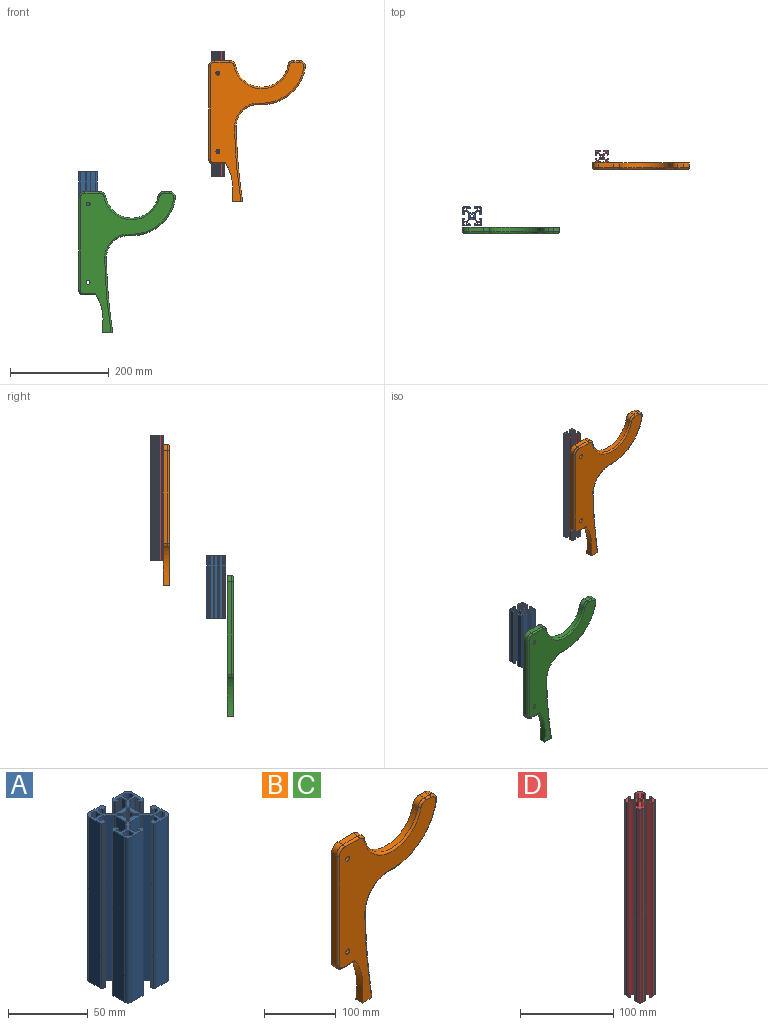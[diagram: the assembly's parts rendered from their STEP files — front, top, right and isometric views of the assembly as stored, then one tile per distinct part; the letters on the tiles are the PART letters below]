
ASSEMBLY  parts=4 mates=2
PART A: 186 faces, bbox 38.1x38.1x127 mm
  f0: plane 127x2.34mm, normal (0,1,0), area 296.8mm2, adj f1,f7,f182,f184
  f1: cylinder r=0.25mm len=127mm, axis (0,0,1), area 50.7mm2, adj f0,f2,f182,f184
  f2: plane 127x4.88mm, normal (1,0,0), area 619.4mm2, adj f1,f3,f182,f184
  f3: cylinder r=0.25mm len=127mm, axis (0,0,1), area 50.7mm2, adj f2,f4,f182,f184
  f4: plane 127x4.88mm, normal (0,-1,0), area 619.4mm2, adj f3,f5,f182,f184
  f5: cylinder r=0.25mm len=127mm, axis (0,0,1), area 50.7mm2, adj f4,f6,f182,f184
  f6: plane 127x2.34mm, normal (-1,0,0), area 296.8mm2, adj f5,f7,f182,f184
  f7: cylinder r=2.79mm len=127mm, axis (0,0,1), area 557.4mm2, adj f0,f6,f182,f184
  f8: plane 127x3.56mm, normal (0,1,0), area 452.4mm2, adj f9,f127,f182,f184
  f9: cylinder r=0.89mm len=127mm, axis (0,0,1), area 177.3mm2, adj f8,f10,f182,f184
  f10: plane 127x2.29mm, normal (1,0,0), area 290.3mm2, adj f9,f11,f182,f184
  f11: cylinder r=0.25mm len=127mm, axis (0,0,1), area 50.7mm2, adj f10,f12,f182,f184
  f12: plane 127x1.35mm, normal (0,-1,0), area 171mm2, adj f11,f13,f182,f184
  f13: cylinder r=0.25mm len=127mm, axis (0,0,1), area 50.7mm2, adj f12,f14,f182,f184
  f14: plane 127x0.98mm, normal (1,0,0), area 124.3mm2, adj f13,f15,f182,f184
  f15: cylinder r=1.57mm len=127mm, axis (0,0,1), area 314.2mm2, adj f14,f16,f182,f184
  f16: plane 127x0.91mm, normal (0,1,0), area 116.1mm2, adj f15,f17,f182,f184
  f17: cylinder r=1.57mm len=127mm, axis (0,0,1), area 314.2mm2, adj f16,f18,f182,f184
  f18: plane 127x10.24mm, normal (-1,0,0), area 1300mm2, adj f17,f19,f182,f184
  f19: cylinder r=3.17mm len=127mm, axis (0,0,1), area 633.4mm2, adj f18,f20,f182,f184
  f20: plane 127x10.24mm, normal (0,-1,0), area 1300mm2, adj f19,f21,f182,f184
  f21: cylinder r=1.57mm len=127mm, axis (0,0,1), area 314.2mm2, adj f20,f22,f182,f184
  f22: plane 127x0.91mm, normal (1,0,0), area 116.1mm2, adj f21,f23,f182,f184
  f23: cylinder r=1.57mm len=127mm, axis (0,0,1), area 314.2mm2, adj f22,f24,f182,f184
  f24: plane 127x0.98mm, normal (0,1,0), area 124.3mm2, adj f23,f25,f182,f184
  f25: cylinder r=0.25mm len=127mm, axis (0,0,1), area 50.7mm2, adj f24,f26,f182,f184
  f26: plane 127x1.35mm, normal (-1,0,0), area 171mm2, adj f25,f27,f182,f184
  f27: cylinder r=0.25mm len=127mm, axis (0,0,1), area 50.7mm2, adj f26,f28,f182,f184
  f28: plane 127x2.29mm, normal (0,1,0), area 290.3mm2, adj f27,f29,f182,f184
  f29: cylinder r=0.89mm len=127mm, axis (0,0,1), area 177.3mm2, adj f28,f30,f182,f184
  f30: plane 127x3.56mm, normal (1,0,0), area 452.4mm2, adj f29,f31,f182,f184
  f31: cylinder r=1.27mm len=127mm, axis (0,0,1), area 126.7mm2, adj f30,f32,f182,f184
  f32: plane 127x4.38mm, normal (0.71,-0.71,0), area 785.9mm2, adj f31,f33,f182,f184
  f33: cylinder r=1.27mm len=127mm, axis (0,0,1), area 126.7mm2, adj f32,f34,f182,f184
  f34: plane 127x9.31mm, normal (0,-1,0), area 1182.4mm2, adj f33,f35,f182,f184
  f35: cylinder r=1.27mm len=127mm, axis (0,0,1), area 126.7mm2, adj f34,f36,f182,f184
  f36: plane 127x4.38mm, normal (-0.71,-0.71,0), area 785.9mm2, adj f35,f37,f182,f184
  f37: cylinder r=1.27mm len=127mm, axis (0,0,1), area 126.7mm2, adj f36,f38,f182,f184
  f38: plane 127x3.56mm, normal (-1,0,0), area 452.4mm2, adj f37,f39,f182,f184
  f39: cylinder r=0.89mm len=127mm, axis (0,0,1), area 177.3mm2, adj f38,f40,f182,f184
  f40: plane 127x2.29mm, normal (0,1,0), area 290.3mm2, adj f39,f41,f182,f184
  f41: cylinder r=0.25mm len=127mm, axis (0,0,1), area 50.7mm2, adj f40,f42,f182,f184
  f42: plane 127x1.35mm, normal (1,0,0), area 171mm2, adj f41,f43,f182,f184
  f43: cylinder r=0.25mm len=127mm, axis (0,0,1), area 50.7mm2, adj f42,f44,f182,f184
  f44: plane 127x0.98mm, normal (0,1,0), area 124.3mm2, adj f43,f45,f182,f184
  f45: cylinder r=1.57mm len=127mm, axis (0,0,1), area 314.2mm2, adj f44,f46,f182,f184
  f46: plane 127x0.91mm, normal (-1,0,0), area 116.1mm2, adj f45,f47,f182,f184
  f47: cylinder r=1.57mm len=127mm, axis (0,0,1), area 314.2mm2, adj f46,f48,f182,f184
  f48: plane 127x10.24mm, normal (0,-1,0), area 1300mm2, adj f47,f49,f182,f184
  f49: cylinder r=3.17mm len=127mm, axis (0,0,1), area 633.4mm2, adj f48,f50,f182,f184
  f50: plane 127x10.24mm, normal (1,0,0), area 1300mm2, adj f49,f51,f182,f184
  f51: cylinder r=1.57mm len=127mm, axis (0,0,1), area 314.2mm2, adj f50,f52,f182,f184
  f52: plane 127x0.91mm, normal (0,1,0), area 116.1mm2, adj f51,f53,f182,f184
  f53: cylinder r=1.57mm len=127mm, axis (0,0,1), area 314.2mm2, adj f52,f54,f182,f184
  f54: plane 127x0.98mm, normal (-1,0,0), area 124.3mm2, adj f53,f55,f182,f184
  f55: cylinder r=0.25mm len=127mm, axis (0,0,1), area 50.7mm2, adj f54,f56,f182,f184
  f56: plane 127x1.35mm, normal (0,-1,0), area 171mm2, adj f55,f57,f182,f184
  f57: cylinder r=0.25mm len=127mm, axis (0,0,1), area 50.7mm2, adj f56,f58,f182,f184
  f58: plane 127x2.29mm, normal (-1,0,0), area 290.3mm2, adj f57,f59,f182,f184
  f59: cylinder r=0.89mm len=127mm, axis (0,0,1), area 177.3mm2, adj f58,f60,f182,f184
  f60: plane 127x3.56mm, normal (0,1,0), area 452.4mm2, adj f59,f61,f182,f184
  f61: cylinder r=1.27mm len=127mm, axis (0,0,1), area 126.7mm2, adj f60,f62,f182,f184
  f62: plane 127x4.38mm, normal (0.71,0.71,0), area 785.9mm2, adj f61,f63,f182,f184
  f63: cylinder r=1.27mm len=127mm, axis (0,0,1), area 126.7mm2, adj f62,f64,f182,f184
  f64: plane 127x9.31mm, normal (1,0,0), area 1182.4mm2, adj f63,f65,f182,f184
  f65: cylinder r=1.27mm len=127mm, axis (0,0,1), area 126.7mm2, adj f64,f66,f182,f184
  f66: plane 127x4.38mm, normal (0.71,-0.71,0), area 785.9mm2, adj f65,f67,f182,f184
  f67: cylinder r=1.27mm len=127mm, axis (0,0,1), area 126.7mm2, adj f66,f68,f182,f184
  f68: plane 127x3.56mm, normal (0,-1,0), area 452.4mm2, adj f67,f69,f182,f184
  f69: cylinder r=0.89mm len=127mm, axis (0,0,1), area 177.3mm2, adj f68,f70,f182,f184
  f70: plane 127x2.29mm, normal (-1,0,0), area 290.3mm2, adj f69,f71,f182,f184
  f71: cylinder r=0.25mm len=127mm, axis (0,0,1), area 50.7mm2, adj f70,f72,f182,f184
  f72: plane 127x1.35mm, normal (0,1,0), area 171mm2, adj f71,f73,f182,f184
  f73: cylinder r=0.25mm len=127mm, axis (0,0,1), area 50.7mm2, adj f72,f74,f182,f184
  f74: plane 127x0.98mm, normal (-1,0,0), area 124.3mm2, adj f73,f75,f182,f184
  f75: cylinder r=1.57mm len=127mm, axis (0,0,1), area 314.2mm2, adj f74,f76,f182,f184
  f76: plane 127x0.91mm, normal (0,-1,0), area 116.1mm2, adj f75,f77,f182,f184
  f77: cylinder r=1.57mm len=127mm, axis (0,0,1), area 314.2mm2, adj f76,f78,f182,f184
  f78: plane 127x10.24mm, normal (1,0,0), area 1300mm2, adj f77,f79,f182,f184
  f79: cylinder r=3.17mm len=127mm, axis (0,0,1), area 633.4mm2, adj f78,f80,f182,f184
  f80: plane 127x10.24mm, normal (0,1,0), area 1300mm2, adj f79,f81,f182,f184
  f81: cylinder r=1.57mm len=127mm, axis (0,0,1), area 314.2mm2, adj f80,f82,f182,f184
  f82: plane 127x0.91mm, normal (-1,0,0), area 116.1mm2, adj f81,f83,f182,f184
  f83: cylinder r=1.57mm len=127mm, axis (0,0,1), area 314.2mm2, adj f82,f84,f182,f184
  f84: plane 127x0.98mm, normal (0,-1,0), area 124.3mm2, adj f83,f85,f182,f184
  f85: cylinder r=0.25mm len=127mm, axis (0,0,1), area 50.7mm2, adj f84,f86,f182,f184
  f86: plane 127x1.35mm, normal (1,0,0), area 171mm2, adj f85,f87,f182,f184
  f87: cylinder r=0.25mm len=127mm, axis (0,0,1), area 50.7mm2, adj f86,f88,f182,f184
  f88: plane 127x2.29mm, normal (0,-1,0), area 290.3mm2, adj f87,f89,f182,f184
  f89: cylinder r=0.89mm len=127mm, axis (0,0,1), area 177.3mm2, adj f88,f90,f182,f184
  f90: plane 127x3.56mm, normal (-1,0,0), area 452.4mm2, adj f89,f91,f182,f184
  f91: cylinder r=1.27mm len=127mm, axis (0,0,1), area 126.7mm2, adj f90,f92,f182,f184
  f92: plane 127x4.38mm, normal (-0.71,0.71,0), area 785.9mm2, adj f91,f93,f182,f184
  f93: cylinder r=1.27mm len=127mm, axis (0,0,1), area 126.7mm2, adj f92,f94,f182,f184
  f94: plane 127x9.31mm, normal (0,1,0), area 1182.4mm2, adj f93,f95,f182,f184
  f95: cylinder r=1.27mm len=127mm, axis (0,0,1), area 126.7mm2, adj f94,f96,f182,f184
  f96: plane 127x4.38mm, normal (0.71,0.71,0), area 785.9mm2, adj f95,f97,f182,f184
  f97: cylinder r=1.27mm len=127mm, axis (0,0,1), area 126.7mm2, adj f96,f98,f182,f184
  f98: plane 127x3.56mm, normal (1,0,0), area 452.4mm2, adj f97,f99,f182,f184
  f99: cylinder r=0.89mm len=127mm, axis (0,0,1), area 177.3mm2, adj f98,f100,f182,f184
  f100: plane 127x2.29mm, normal (0,-1,0), area 290.3mm2, adj f99,f101,f182,f184
  f101: cylinder r=0.25mm len=127mm, axis (0,0,1), area 50.7mm2, adj f100,f102,f182,f184
  f102: plane 127x1.35mm, normal (-1,0,0), area 171mm2, adj f101,f103,f182,f184
  f103: cylinder r=0.25mm len=127mm, axis (0,0,1), area 50.7mm2, adj f102,f104,f182,f184
  f104: plane 127x0.98mm, normal (0,-1,0), area 124.3mm2, adj f103,f105,f182,f184
  f105: cylinder r=1.57mm len=127mm, axis (0,0,1), area 314.2mm2, adj f104,f106,f182,f184
  f106: plane 127x0.91mm, normal (1,0,0), area 116.1mm2, adj f105,f107,f182,f184
  f107: cylinder r=1.57mm len=127mm, axis (0,0,1), area 314.2mm2, adj f106,f108,f182,f184
  f108: plane 127x10.24mm, normal (0,1,0), area 1300mm2, adj f107,f109,f182,f184
  f109: cylinder r=3.17mm len=127mm, axis (0,0,1), area 633.4mm2, adj f108,f110,f182,f184
  f110: plane 127x10.24mm, normal (-1,0,0), area 1300mm2, adj f109,f111,f182,f184
  f111: cylinder r=1.57mm len=127mm, axis (0,0,1), area 314.2mm2, adj f110,f112,f182,f184
  f112: plane 127x0.91mm, normal (0,-1,0), area 116.1mm2, adj f111,f113,f182,f184
  f113: cylinder r=1.57mm len=127mm, axis (0,0,1), area 314.2mm2, adj f112,f114,f182,f184
  f114: plane 127x0.98mm, normal (1,0,0), area 124.3mm2, adj f113,f115,f182,f184
  f115: cylinder r=0.25mm len=127mm, axis (0,0,1), area 50.7mm2, adj f114,f116,f182,f184
  f116: plane 127x1.35mm, normal (0,1,0), area 171mm2, adj f115,f117,f182,f184
  f117: cylinder r=0.25mm len=127mm, axis (0,0,1), area 50.7mm2, adj f116,f118,f182,f184
  f118: plane 127x2.29mm, normal (1,0,0), area 290.3mm2, adj f117,f119,f182,f184
  f119: cylinder r=0.89mm len=127mm, axis (0,0,1), area 177.3mm2, adj f118,f120,f182,f184
  f120: plane 127x3.56mm, normal (0,-1,0), area 452.4mm2, adj f119,f121,f182,f184
  f121: cylinder r=1.27mm len=127mm, axis (0,0,1), area 126.7mm2, adj f120,f122,f182,f184
  f122: plane 127x4.38mm, normal (-0.71,-0.71,0), area 785.9mm2, adj f121,f123,f182,f184
  f123: cylinder r=1.27mm len=127mm, axis (0,0,1), area 126.7mm2, adj f122,f124,f182,f184
  f124: plane 127x9.31mm, normal (-1,0,0), area 1182.4mm2, adj f123,f125,f182,f184
  f125: cylinder r=1.27mm len=127mm, axis (0,0,1), area 126.7mm2, adj f124,f126,f182,f184
  f126: plane 127x4.38mm, normal (-0.71,0.71,0), area 785.9mm2, adj f125,f127,f182,f184
  f127: cylinder r=1.27mm len=127mm, axis (0,0,1), area 126.7mm2, adj f8,f126,f182,f184
  f128: plane 127x4.88mm, normal (0,1,0), area 619.4mm2, adj f129,f135,f182,f184
  f129: cylinder r=0.25mm len=127mm, axis (0,0,1), area 50.7mm2, adj f128,f130,f182,f184
  f130: plane 127x2.34mm, normal (1,0,0), area 296.8mm2, adj f129,f131,f182,f184
  f131: cylinder r=2.79mm len=127mm, axis (0,0,1), area 557.4mm2, adj f130,f132,f182,f184
  f132: plane 127x2.34mm, normal (0,-1,0), area 296.8mm2, adj f131,f133,f182,f184
  f133: cylinder r=0.25mm len=127mm, axis (0,0,1), area 50.7mm2, adj f132,f134,f182,f184
  f134: plane 127x4.88mm, normal (-1,0,0), area 619.4mm2, adj f133,f135,f182,f184
  f135: cylinder r=0.25mm len=127mm, axis (0,0,1), area 50.7mm2, adj f128,f134,f182,f184
  f136: plane 127x4.88mm, normal (-1,0,0), area 619.4mm2, adj f137,f143,f182,f184
  f137: cylinder r=0.25mm len=127mm, axis (0,0,1), area 50.7mm2, adj f136,f138,f182,f184
  f138: plane 127x2.34mm, normal (0,1,0), area 296.8mm2, adj f137,f139,f182,f184
  f139: cylinder r=2.79mm len=127mm, axis (0,0,1), area 557.4mm2, adj f138,f140,f182,f184
  f140: plane 127x2.34mm, normal (1,0,0), area 296.8mm2, adj f139,f141,f182,f184
  f141: cylinder r=0.25mm len=127mm, axis (0,0,1), area 50.7mm2, adj f140,f142,f182,f184
  f142: plane 127x4.88mm, normal (0,-1,0), area 619.4mm2, adj f141,f143,f182,f184
  f143: cylinder r=0.25mm len=127mm, axis (0,0,1), area 50.7mm2, adj f136,f142,f182,f184
  f144: plane 127x1.89mm, normal (0.71,-0.71,0), area 339.6mm2, adj f145,f175,f182,f184
  f145: cylinder r=3.33mm len=127mm, axis (0,0,1), area 367.4mm2, adj f144,f146,f182,f184
  f146: plane 127x1.89mm, normal (0.71,0.71,0), area 339.6mm2, adj f145,f147,f182,f184
  f147: cylinder r=0.89mm len=127mm, axis (0,0,1), area 88.7mm2, adj f146,f148,f182,f184
  f148: plane 127x0.99mm, normal (1,0,0), area 126.3mm2, adj f147,f149,f182,f184
  f149: cylinder r=0.25mm len=127mm, axis (0,0,1), area 50.7mm2, adj f148,f150,f182,f184
  f150: plane 127x0.99mm, normal (0,-1,0), area 126.3mm2, adj f149,f151,f182,f184
  f151: cylinder r=0.89mm len=127mm, axis (0,0,1), area 88.7mm2, adj f150,f152,f182,f184
  f152: plane 127x1.89mm, normal (-0.71,-0.71,0), area 339.6mm2, adj f151,f153,f182,f184
  f153: cylinder r=3.33mm len=127mm, axis (0,0,1), area 367.4mm2, adj f152,f154,f182,f184
  f154: plane 127x1.89mm, normal (0.71,-0.71,0), area 339.6mm2, adj f153,f155,f182,f184
  f155: cylinder r=0.89mm len=127mm, axis (0,0,1), area 88.7mm2, adj f154,f156,f182,f184
  f156: plane 127x0.99mm, normal (0,-1,0), area 126.3mm2, adj f155,f157,f182,f184
  f157: cylinder r=0.25mm len=127mm, axis (0,0,1), area 50.7mm2, adj f156,f158,f182,f184
  f158: plane 127x0.99mm, normal (-1,0,0), area 126.3mm2, adj f157,f159,f182,f184
  f159: cylinder r=0.89mm len=127mm, axis (0,0,1), area 88.7mm2, adj f158,f160,f182,f184
  f160: plane 127x1.89mm, normal (-0.71,0.71,0), area 339.6mm2, adj f159,f161,f182,f184
  f161: cylinder r=3.33mm len=127mm, axis (0,0,1), area 367.4mm2, adj f160,f162,f182,f184
  f162: plane 127x1.89mm, normal (-0.71,-0.71,0), area 339.6mm2, adj f161,f163,f182,f184
  f163: cylinder r=0.89mm len=127mm, axis (0,0,1), area 88.7mm2, adj f162,f164,f182,f184
  f164: plane 127x0.99mm, normal (-1,0,0), area 126.3mm2, adj f163,f165,f182,f184
  f165: cylinder r=0.25mm len=127mm, axis (0,0,1), area 50.7mm2, adj f164,f166,f182,f184
  f166: plane 127x0.99mm, normal (0,1,0), area 126.3mm2, adj f165,f167,f182,f184
  f167: cylinder r=0.89mm len=127mm, axis (0,0,1), area 88.7mm2, adj f166,f168,f182,f184
  f168: plane 127x1.89mm, normal (0.71,0.71,0), area 339.6mm2, adj f167,f169,f182,f184
  f169: cylinder r=3.33mm len=127mm, axis (0,0,1), area 367.4mm2, adj f168,f170,f182,f184
  f170: plane 127x1.89mm, normal (-0.71,0.71,0), area 339.6mm2, adj f169,f171,f182,f184
  f171: cylinder r=0.89mm len=127mm, axis (0,0,1), area 88.7mm2, adj f170,f172,f182,f184
  f172: plane 127x0.99mm, normal (0,1,0), area 126.3mm2, adj f171,f173,f182,f184
  f173: cylinder r=0.25mm len=127mm, axis (0,0,1), area 50.7mm2, adj f172,f174,f182,f184
  f174: plane 127x0.99mm, normal (1,0,0), area 126.3mm2, adj f173,f175,f182,f184
  f175: cylinder r=0.89mm len=127mm, axis (0,0,1), area 88.7mm2, adj f144,f174,f182,f184
  f176: plane 127x4.88mm, normal (0,1,0), area 619.4mm2, adj f177,f181,f182,f184
  f177: cylinder r=0.25mm len=127mm, axis (0,0,1), area 50.7mm2, adj f176,f178,f182,f184
  f178: plane 127x4.88mm, normal (1,0,0), area 619.4mm2, adj f177,f179,f182,f184
  f179: cylinder r=0.25mm len=127mm, axis (0,0,1), area 50.7mm2, adj f178,f180,f182,f184
  f180: plane 127x2.34mm, normal (0,-1,0), area 296.8mm2, adj f179,f182,f183,f184
  f181: cylinder r=0.25mm len=127mm, axis (0,0,1), area 50.7mm2, adj f176,f182,f184,f185
  f182: plane 38.1x38.1mm, normal (0,0,-1), area 503.5mm2, adj f0,f1,f2,f3,f4,f5,f6,f7
  f183: cylinder r=2.79mm len=127mm, axis (0,0,1), area 557.4mm2, adj f180,f182,f184,f185
  f184: plane 38.1x38.1mm, normal (0,0,1), area 503.5mm2, adj f0,f1,f2,f3,f4,f5,f6,f7
  f185: plane 127x2.34mm, normal (-1,0,0), area 296.8mm2, adj f181,f182,f183,f184
PART B: 32 faces, bbox 204.5x12.9x294.3 mm
  f0: plane 10.34x9.53mm, normal (0,0,1), area 98.5mm2, adj f11,f14,f17,f27
  f1: cylinder r=53.98mm len=105.97mm, axis (0,1,0), area 1418.1mm2, adj f11,f14,f15,f25
  f2: plane 29.54x9.53mm, normal (0,0,1), area 281.4mm2, adj f11,f15,f16,f23
  f3: plane 187.33x9.53mm, normal (-1,0,0), area 1784.3mm2, adj f11,f16,f18,f21
  f4: plane 25.4x9.53mm, normal (0,0,-1), area 241.9mm2, adj f5,f11,f18,f19
  f5: extruded ~80.14x16.78mm, area 1020mm2, adj f4,f6,f10,f11,f19
  f6: plane 21.03x12.9mm, normal (0,0,-1), area 262.3mm2, adj f5,f7,f10,f11,f31
  f7: extruded ~152.4x12.85mm, area 1458mm2, adj f6,f8,f11,f31
  f8: cylinder r=44.74mm len=47.03mm, axis (0,1,0), area 691.2mm2, adj f7,f9,f11,f30
  f9: cylinder r=89.55mm len=92.92mm, axis (0,1,0), area 1242mm2, adj f8,f11,f17,f29
  f10: plane 283.35x189.84mm, normal (0,-1,0), area 17052.7mm2, adj f5,f6,f12,f13,f19,f20,f21,f22
  f11: plane 286.51x196.19mm, normal (0,1,0), area 19722.5mm2, adj f0,f1,f2,f3,f4,f5,f6,f7
  f12: cylinder r=3.97mm len=12.7mm, axis (0,-1,0), area 316.7mm2, adj f10,f11
  f13: cylinder r=3.97mm len=12.7mm, axis (0,-1,0), area 316.7mm2, adj f10,f11
  f14: cylinder r=12.7mm len=12.47mm, axis (0,1,0), area 166.8mm2, adj f0,f1,f11,f26
  f15: cylinder r=12.7mm len=12.47mm, axis (0,1,0), area 166.8mm2, adj f1,f2,f11,f24
  f16: cylinder r=12.7mm len=12.7mm, axis (0,1,0), area 190mm2, adj f2,f3,f11,f22
  f17: cylinder r=12.7mm len=14.8mm, axis (0,1,0), area 210.1mm2, adj f0,f9,f11,f28
  f18: cylinder r=9.53mm len=9.53mm, axis (0,-1,0), area 142.5mm2, adj f3,f4,f11,f20
  f19: cylinder r=3.17mm len=25.4mm, axis (-1,0,0), area 121mm2, adj f4,f5,f10,f20
  f20: torus R=6.35mm, axis (0,-1,0), area 65.6mm2, adj f10,f18,f19,f21
  f21: cylinder r=3.17mm len=187.33mm, axis (0,0,1), area 934.2mm2, adj f3,f10,f20,f22
  f22: torus R=9.53mm, axis (0,-1,0), area 90.5mm2, adj f10,f16,f21,f23
  f23: cylinder r=3.17mm len=29.54mm, axis (1,0,0), area 147.3mm2, adj f2,f10,f22,f24
  f24: torus R=9.53mm, axis (0,-1,0), area 79.4mm2, adj f10,f15,f23,f25
  f25: torus R=57.15mm, axis (0,-1,0), area 758.4mm2, adj f1,f10,f24,f26
  f26: torus R=9.53mm, axis (0,-1,0), area 79.4mm2, adj f10,f14,f25,f27
  f27: cylinder r=3.17mm len=10.34mm, axis (1,0,0), area 51.6mm2, adj f0,f10,f26,f28
  f28: torus R=9.53mm, axis (0,-1,0), area 100mm2, adj f10,f17,f27,f29
  f29: torus R=86.38mm, axis (0,-1,0), area 642mm2, adj f9,f10,f28,f30
  f30: torus R=47.91mm, axis (0,-1,0), area 371.2mm2, adj f8,f10,f29,f31
  f31: bspline ~188.6x16.91mm, area 763.1mm2, adj f6,f7,f10,f30
PART C: same geometry as B
PART D: 83 faces, bbox 25.4x25.4x254 mm
  f0: cylinder r=3.17mm len=254mm, axis (0,0,1), area 633.4mm2, adj f1,f79,f80,f81
  f1: plane 254x3.24mm, normal (-1,0,0), area 822mm2, adj f0,f2,f80,f81
  f2: cylinder r=3.17mm len=254mm, axis (0,0,1), area 633.4mm2, adj f1,f3,f80,f81
  f3: plane 254x3.33mm, normal (-0.71,0.71,0), area 1196.2mm2, adj f2,f4,f80,f81
  f4: cylinder r=1.02mm len=254mm, axis (0,0,1), area 608mm2, adj f3,f5,f80,f81
  f5: plane 254x2.13mm, normal (1,0,0), area 541.4mm2, adj f4,f6,f80,f81
  f6: cylinder r=1.1mm len=254mm, axis (0,0,1), area 881.7mm2, adj f5,f7,f80,f81
  f7: plane 254x0.97mm, normal (-1,0,0), area 247.3mm2, adj f6,f8,f80,f81
  f8: cylinder r=0.51mm len=254mm, axis (0,0,1), area 405.4mm2, adj f7,f9,f80,f81
  f9: plane 254x3.22mm, normal (-1,0,0), area 817.2mm2, adj f8,f10,f80,f81
  f10: cylinder r=0.51mm len=254mm, axis (0,0,1), area 405.3mm2, adj f9,f11,f80,f81
  f11: cylinder r=2.11mm len=254mm, axis (0,0,1), area 854mm2, adj f10,f12,f80,f81
  f12: cylinder r=0.51mm len=254mm, axis (0,0,1), area 405.3mm2, adj f11,f13,f80,f81
  f13: plane 254x3.22mm, normal (0,-1,0), area 817.2mm2, adj f12,f14,f80,f81
  f14: cylinder r=0.51mm len=254mm, axis (0,0,1), area 405.4mm2, adj f13,f15,f80,f81
  f15: plane 254x0.97mm, normal (0,-1,0), area 247.3mm2, adj f14,f16,f80,f81
  f16: cylinder r=1.1mm len=254mm, axis (0,0,1), area 881.7mm2, adj f15,f17,f80,f81
  f17: plane 254x2.13mm, normal (0,1,0), area 541.4mm2, adj f16,f18,f80,f81
  f18: cylinder r=1.02mm len=254mm, axis (0,0,1), area 608mm2, adj f17,f19,f80,f81
  f19: plane 254x3.33mm, normal (0.71,-0.71,0), area 1196.2mm2, adj f18,f20,f80,f81
  f20: cylinder r=3.17mm len=254mm, axis (0,0,1), area 633.4mm2, adj f19,f21,f80,f81
  f21: plane 254x3.24mm, normal (0,-1,0), area 822mm2, adj f20,f22,f80,f81
  f22: cylinder r=3.17mm len=254mm, axis (0,0,1), area 633.4mm2, adj f21,f23,f80,f81
  f23: plane 254x3.33mm, normal (-0.71,-0.71,0), area 1196.2mm2, adj f22,f24,f80,f81
  f24: cylinder r=1.02mm len=254mm, axis (0,0,1), area 608mm2, adj f23,f25,f80,f81
  f25: plane 254x2.13mm, normal (0,1,0), area 541.4mm2, adj f24,f26,f80,f81
  f26: cylinder r=1.1mm len=254mm, axis (0,0,1), area 881.7mm2, adj f25,f27,f80,f81
  f27: plane 254x0.97mm, normal (0,-1,0), area 247.3mm2, adj f26,f28,f80,f81
  f28: cylinder r=0.51mm len=254mm, axis (0,0,1), area 405.4mm2, adj f27,f29,f80,f81
  f29: plane 254x3.22mm, normal (0,-1,0), area 817.2mm2, adj f28,f30,f80,f81
  f30: cylinder r=0.51mm len=254mm, axis (0,0,1), area 405.3mm2, adj f29,f31,f80,f81
  f31: cylinder r=2.11mm len=254mm, axis (0,0,1), area 854mm2, adj f30,f32,f80,f81
  f32: cylinder r=0.51mm len=254mm, axis (0,0,1), area 405.3mm2, adj f31,f33,f80,f81
  f33: plane 254x3.22mm, normal (1,0,0), area 817.2mm2, adj f32,f34,f80,f81
  f34: cylinder r=0.51mm len=254mm, axis (0,0,1), area 405.4mm2, adj f33,f35,f80,f81
  f35: plane 254x0.97mm, normal (1,0,0), area 247.3mm2, adj f34,f36,f80,f81
  f36: cylinder r=1.1mm len=254mm, axis (0,0,1), area 881.7mm2, adj f35,f37,f80,f81
  f37: plane 254x2.13mm, normal (-1,0,0), area 541.4mm2, adj f36,f38,f80,f81
  f38: cylinder r=1.02mm len=254mm, axis (0,0,1), area 608mm2, adj f37,f39,f80,f81
  f39: plane 254x3.33mm, normal (0.71,0.71,0), area 1196.2mm2, adj f38,f40,f80,f81
  f40: cylinder r=3.17mm len=254mm, axis (0,0,1), area 633.4mm2, adj f39,f41,f80,f81
  f41: plane 254x3.24mm, normal (1,0,0), area 822mm2, adj f40,f42,f80,f81
  f42: cylinder r=3.17mm len=254mm, axis (0,0,1), area 633.4mm2, adj f41,f43,f80,f81
  f43: plane 254x3.33mm, normal (0.71,-0.71,0), area 1196.2mm2, adj f42,f44,f80,f81
  f44: cylinder r=1.02mm len=254mm, axis (0,0,1), area 608mm2, adj f43,f45,f80,f81
  f45: plane 254x2.13mm, normal (-1,0,0), area 541.4mm2, adj f44,f46,f80,f81
  f46: cylinder r=1.1mm len=254mm, axis (0,0,1), area 881.7mm2, adj f45,f47,f80,f81
  f47: plane 254x0.97mm, normal (1,0,0), area 247.3mm2, adj f46,f48,f80,f81
  f48: cylinder r=0.51mm len=254mm, axis (0,0,1), area 405.4mm2, adj f47,f49,f80,f81
  f49: plane 254x3.22mm, normal (1,0,0), area 817.2mm2, adj f48,f50,f80,f81
  f50: cylinder r=0.51mm len=254mm, axis (0,0,1), area 405.3mm2, adj f49,f51,f80,f81
  f51: cylinder r=2.11mm len=254mm, axis (0,0,1), area 854mm2, adj f50,f52,f80,f81
  f52: cylinder r=0.51mm len=254mm, axis (0,0,1), area 405.3mm2, adj f51,f53,f80,f81
  f53: plane 254x3.22mm, normal (0,1,0), area 817.2mm2, adj f52,f54,f80,f81
  f54: cylinder r=0.51mm len=254mm, axis (0,0,1), area 405.4mm2, adj f53,f55,f80,f81
  f55: plane 254x0.97mm, normal (0,1,0), area 247.3mm2, adj f54,f56,f80,f81
  f56: cylinder r=1.1mm len=254mm, axis (0,0,1), area 881.7mm2, adj f55,f57,f80,f81
  f57: plane 254x2.13mm, normal (0,-1,0), area 541.4mm2, adj f56,f58,f80,f81
  f58: cylinder r=1.02mm len=254mm, axis (0,0,1), area 608mm2, adj f57,f59,f80,f81
  f59: plane 254x3.33mm, normal (-0.71,0.71,0), area 1196.2mm2, adj f58,f60,f80,f81
  f60: cylinder r=3.17mm len=254mm, axis (0,0,1), area 633.4mm2, adj f59,f61,f80,f81
  f61: plane 254x3.24mm, normal (0,1,0), area 822mm2, adj f60,f62,f80,f81
  f62: cylinder r=3.17mm len=254mm, axis (0,0,1), area 633.4mm2, adj f61,f63,f80,f81
  f63: plane 254x3.33mm, normal (0.71,0.71,0), area 1196.2mm2, adj f62,f64,f80,f81
  f64: cylinder r=1.02mm len=254mm, axis (0,0,1), area 608mm2, adj f63,f65,f80,f81
  f65: plane 254x2.13mm, normal (0,-1,0), area 541.4mm2, adj f64,f66,f80,f81
  f66: cylinder r=1.1mm len=254mm, axis (0,0,1), area 881.7mm2, adj f65,f67,f80,f81
  f67: plane 254x0.97mm, normal (0,1,0), area 247.3mm2, adj f66,f68,f80,f81
  f68: cylinder r=0.51mm len=254mm, axis (0,0,1), area 405.4mm2, adj f67,f69,f80,f81
  f69: plane 254x3.22mm, normal (0,1,0), area 817.2mm2, adj f68,f70,f80,f81
  f70: cylinder r=0.51mm len=254mm, axis (0,0,1), area 405.3mm2, adj f69,f71,f80,f81
  f71: cylinder r=2.11mm len=254mm, axis (0,0,1), area 854mm2, adj f70,f72,f80,f81
  f72: cylinder r=0.51mm len=254mm, axis (0,0,1), area 405.3mm2, adj f71,f73,f80,f81
  f73: plane 254x3.22mm, normal (-1,0,0), area 817.2mm2, adj f72,f74,f80,f81
  f74: cylinder r=0.51mm len=254mm, axis (0,0,1), area 405.4mm2, adj f73,f75,f80,f81
  f75: plane 254x0.97mm, normal (-1,0,0), area 247.3mm2, adj f74,f76,f80,f81
  f76: cylinder r=1.1mm len=254mm, axis (0,0,1), area 881.7mm2, adj f75,f77,f80,f81
  f77: plane 254x2.13mm, normal (1,0,0), area 541.4mm2, adj f76,f78,f80,f81
  f78: cylinder r=1.02mm len=254mm, axis (0,0,1), area 608mm2, adj f77,f79,f80,f81
  f79: plane 254x3.33mm, normal (-0.71,-0.71,0), area 1196.2mm2, adj f0,f78,f80,f81
  f80: plane 25.4x25.4mm, normal (0,0,1), area 279.7mm2, adj f0,f1,f2,f3,f4,f5,f6,f7
  f81: plane 25.4x25.4mm, normal (0,0,-1), area 279.7mm2, adj f0,f1,f2,f3,f4,f5,f6,f7
  f82: cylinder r=2.6mm len=254mm, axis (0,0,1), area 4155mm2, adj f80,f81
PLACE A t=(-89.79,56.48,215.46)mm
PLACE B t=(255.12,164.34,307)mm
PLACE C t=(-8.03,34.43,41.67)mm
PLACE D t=(173.2,177.04,460.17)mm
MATE planar B.f11 <-> D.f13  axis (0,1,0) through (216.4,164.34,342.05)mm
MATE planar A.f18 <-> C.f3  axis (-1,0,0) through (-108.84,45.73,151.96)mm
